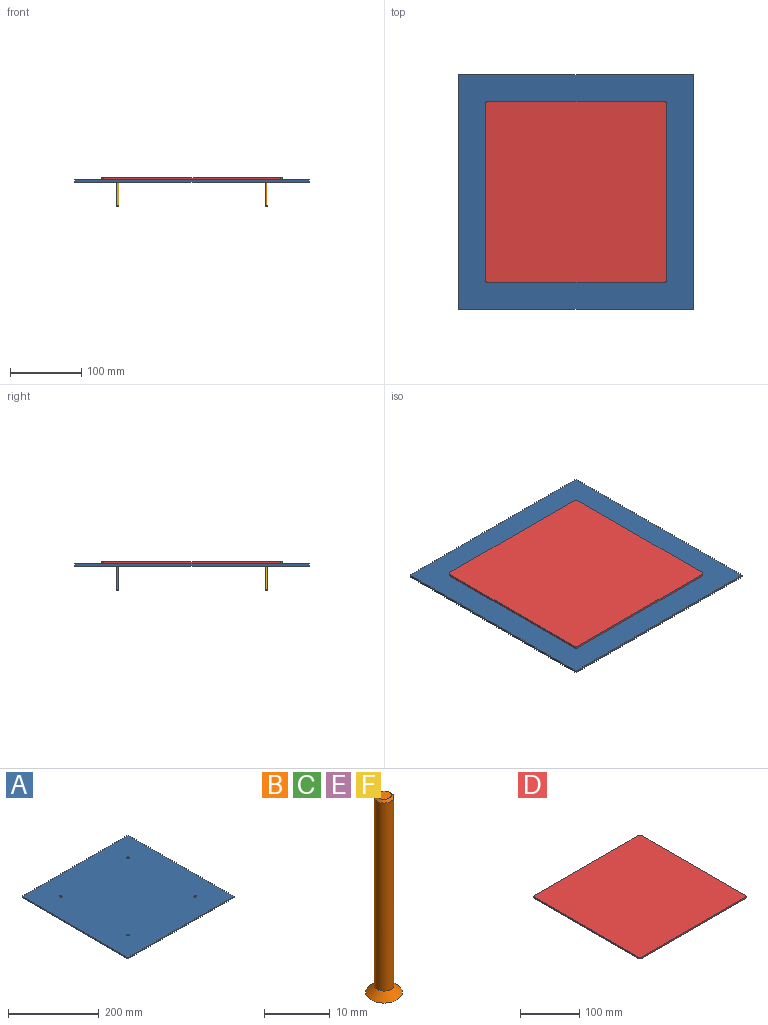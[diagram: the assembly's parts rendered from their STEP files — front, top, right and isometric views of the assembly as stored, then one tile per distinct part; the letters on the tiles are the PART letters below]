
ASSEMBLY  parts=6 mates=5
PART A: 14 faces, bbox 330x330x3 mm
  f0: plane 330x3mm, normal (0,-1,0), area 990mm2, adj f1,f3,f4,f5
  f1: plane 330x3mm, normal (1,0,0), area 990mm2, adj f0,f2,f4,f5
  f2: plane 330x3mm, normal (0,1,0), area 990mm2, adj f1,f3,f4,f5
  f3: plane 330x3mm, normal (-1,0,0), area 990mm2, adj f0,f2,f4,f5
  f4: plane 330x330mm, normal (0,0,1), area 108801.5mm2, adj f0,f1,f2,f3,f10,f11,f12,f13
  f5: plane 330x330mm, normal (0,0,-1), area 108859.3mm2, adj f0,f1,f2,f3,f6,f7,f8,f9
  f6: cylinder r=1.8mm len=3.6mm, axis (0,0,1), area 22.6mm2, adj f5,f10
  f7: cylinder r=1.8mm len=3.6mm, axis (0,0,1), area 22.6mm2, adj f5,f11
  f8: cylinder r=1.8mm len=3.6mm, axis (0,0,1), area 22.6mm2, adj f5,f12
  f9: cylinder r=1.8mm len=3.6mm, axis (0,0,1), area 22.6mm2, adj f5,f13
  f10: cone r=1.8mm half-angle=45deg, axis (0,0,1), area 20.4mm2, adj f4,f6
  f11: cone r=1.8mm half-angle=45deg, axis (0,0,1), area 20.4mm2, adj f4,f7
  f12: cone r=1.8mm half-angle=45deg, axis (0,0,1), area 20.4mm2, adj f4,f8
  f13: cone r=1.8mm half-angle=45deg, axis (0,0,1), area 20.4mm2, adj f4,f9
PART B: 12 faces, bbox 5.6x5.6x36.7 mm
  f0: plane 5.6x5.6mm, normal (0,0,-1), area 16.8mm2, adj f3,f5,f6,f7,f8,f9,f10
  f1: cylinder r=1.5mm len=34.95mm, axis (0,0,-1), area 329.4mm2, adj f3,f4
  f2: plane 2.21x2.21mm, normal (0,0,1), area 3.8mm2, adj f4
  f3: cone r=1.15mm half-angle=45deg, axis (0,0,-1), area 24.8mm2, adj f0,f1
  f4: cone r=1.1mm half-angle=45deg, axis (0,0,-1), area 4.6mm2, adj f1,f2
  f5: plane 1.5x0.87mm, normal (-0.87,0.5,0), area 0.9mm2, adj f0,f6,f10,f11
  f6: plane 1.73x0.5mm, normal (0,1,0), area 0.9mm2, adj f0,f5,f7,f11
  f7: plane 1.5x0.87mm, normal (0.87,0.5,0), area 0.9mm2, adj f0,f6,f8,f11
  f8: plane 1.5x0.87mm, normal (0.87,-0.5,0), area 0.9mm2, adj f0,f7,f9,f11
  f9: plane 1.73x0.5mm, normal (0,-1,0), area 0.9mm2, adj f0,f8,f10,f11
  f10: plane 1.5x0.87mm, normal (-0.87,-0.5,0), area 0.9mm2, adj f0,f5,f9,f11
  f11: plane 3.46x3mm, normal (0,0,-1), area 7.8mm2, adj f5,f6,f7,f8,f9,f10
PART C: same geometry as B
PART D: 10 faces, bbox 254x254x3 mm
  f0: plane 248x3mm, normal (0,-1,0), area 744mm2, adj f4,f5,f6,f9
  f1: plane 248x3mm, normal (1,0,0), area 744mm2, adj f4,f5,f6,f7
  f2: plane 248x3mm, normal (0,1,0), area 744mm2, adj f4,f5,f7,f8
  f3: plane 248x3mm, normal (-1,0,0), area 744mm2, adj f4,f5,f8,f9
  f4: plane 254x254mm, normal (0,0,1), area 64508.3mm2, adj f0,f1,f2,f3,f6,f7,f8,f9
  f5: plane 254x254mm, normal (0,0,-1), area 64508.3mm2, adj f0,f1,f2,f3,f6,f7,f8,f9
  f6: cylinder r=3mm len=3mm, axis (0,0,1), area 14.1mm2, adj f0,f1,f4,f5
  f7: cylinder r=3mm len=3mm, axis (0,0,-1), area 14.1mm2, adj f1,f2,f4,f5
  f8: cylinder r=3mm len=3mm, axis (0,0,1), area 14.1mm2, adj f2,f3,f4,f5
  f9: cylinder r=3mm len=3mm, axis (0,0,-1), area 14.1mm2, adj f0,f3,f4,f5
PART E: same geometry as B
PART F: same geometry as B
PLACE A t=(-32.85,-22.62,-6.98)mm
PLACE B rot(axis=(1,0,0),180deg) t=(71.65,-127.12,-4.18)mm
PLACE C rot(axis=(1,0,0),180deg) t=(71.65,81.88,-4.18)mm
PLACE D rot(axis=(1,0,0),180deg) t=(-32.85,-22.62,-0.98)mm
PLACE E rot(axis=(1,0,0),180deg) t=(-137.35,81.88,-4.18)mm
PLACE F rot(axis=(1,0,0),180deg) t=(-137.35,-127.12,-4.18)mm
MATE fastened F.f1 <-> A.f6  axis (0,0,1) through (-137.35,-127.12,-5.48)mm
MATE fastened E.f1 <-> A.f9  axis (0,0,1) through (-137.35,81.88,-5.48)mm
MATE fastened B.f1 <-> A.f7  axis (0,0,1) through (71.65,-127.12,-5.48)mm
MATE fastened D.f4 <-> A.f4  axis (0,0,-1) through (-32.85,-22.62,-3.98)mm
MATE fastened C.f1 <-> A.f8  axis (0,0,1) through (71.65,81.88,-5.48)mm
